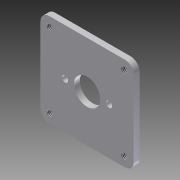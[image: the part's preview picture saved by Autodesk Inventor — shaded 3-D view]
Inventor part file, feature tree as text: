
AUTODESK INVENTOR PART (.ipt)
format: ipt  version: 2012 (Build 160160000, 160)  size: 144,384 bytes
history: native  units: in
note: dims shown in document units (in); Inventor stores cm internally (conversion verified against a paired STEP export)
features: extrude x2, hole x2, sketch x1, fillet x1
ambient origin geometry x8: Origin, YZ Plane, XZ Plane, XY Plane, X Axis, Y Axis, Z Axis, Center Point
bodies: Solid1 (feature_tree)
feature tree (6):
  sketch  "Sketch1"  dims[d0=0.9449in d1=0.4724in d2=1.0236in d3=0.5118in d4=0.0787in d5=0.2559in d6=0.128in d7=0.0787in d8=0.5625in d9=2.0in d10=1.0in d11=2.0in d12=1.0in d13=0.1181in d14=0.3937in d15=0.1575in d16=0.1575in d17=0.1575in d18=0.1575in d19=0.1575in d20=0.2in d21=0.2in d22=0.2in d23=0.2in d24=0.125in d25=0.0in d34=1.6in d35=1.6in d44=0.1875in d53=0.13in d54=0.75in d55=0.375in d56=0.25in d57=0.5635in d58=1.0in d59=0.8108in d61=0.4724in d62=0.4724in d63=1.0in d64=0.0in d65=0.131in d66=0.75in d67=0.375in d68=0.25in d69=0.5635in d70=1.0in d71=0.8108in]
  extrude  "Extrusion1"  Depth=0.4724in
  fillet  "Fillet2"  Radius=1.0236in
  hole  "Hole2"  [1 undecoded]
  extrude  "Extrusion6"  Depth=0.0787in
  hole  "Hole3"  [1 undecoded]
note: 2 required parameter values undecoded (feature->parameter linkage not recoverable at this tier; creation-order binding heuristic only, values carry confidence <= 0.55)
